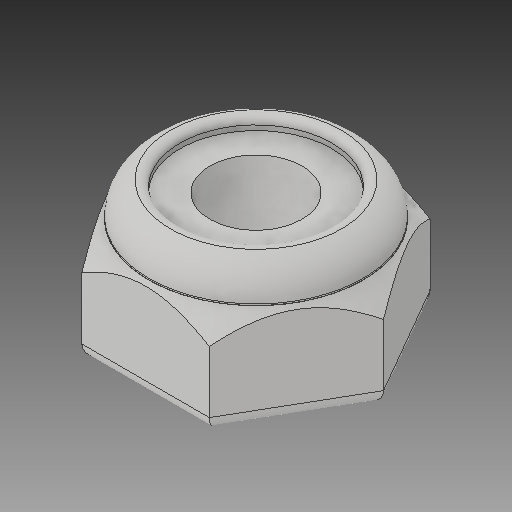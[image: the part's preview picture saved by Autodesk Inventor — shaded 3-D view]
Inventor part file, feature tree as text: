
AUTODESK INVENTOR PART (.ipt)
format: ipt  version: 2017 (Build 210142000, 142)  size: 169,984 bytes
history: native  units: in
note: dims shown in document units (in); Inventor stores cm internally (conversion verified against a paired STEP export)
features: fillet x1
ambient origin geometry x8: Origin, YZ Plane, XZ Plane, XY Plane, X Axis, Y Axis, Z Axis, Center Point
bodies: Solid1 (feature_tree)
feature tree (1):
  fillet  "Fillet5"  [1 undecoded]
note: 1 required parameter value undecoded (feature->parameter linkage not recoverable at this tier; creation-order binding heuristic only, values carry confidence <= 0.55)
